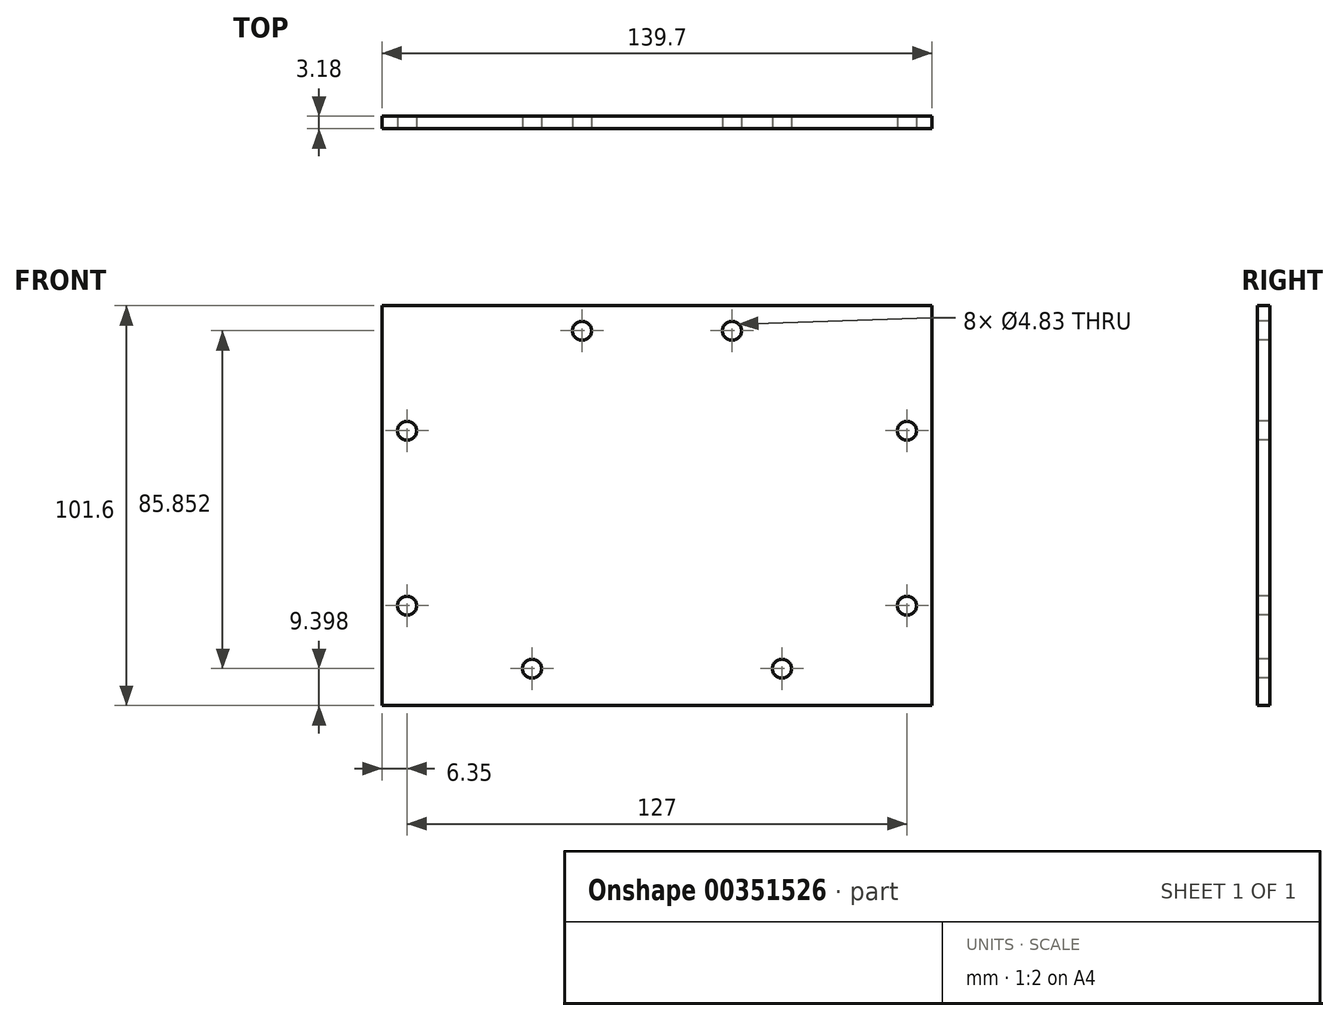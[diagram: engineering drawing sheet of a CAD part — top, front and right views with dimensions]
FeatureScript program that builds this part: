
annotation { "Feature Type Name" : "Feature", "Feature Type Description" : "" }
export const myFeature = defineFeature(function(context is Context, id is Id, definition is map)
    precondition{}
    {
        {
            var Q0;
            Q0=qCreatedBy(makeId("Front.planeOp"),FACE);
            var sketch = newSketch(context, id + "F0", { "sketchPlane" : qUnion([Q0])});
            skLineSegment(sketch, "E0.bottom", {"start": v(69.85, 50.8) * mm, "end": v(-69.85, 50.8) * mm});
            skLineSegment(sketch, "E0.top", {"start": v(69.85, -50.8) * mm, "end": v(-69.85, -50.8) * mm});
            skLineSegment(sketch, "E0.left", {"start": v(69.85, 50.8) * mm, "end": v(69.85, -50.8) * mm});
            skLineSegment(sketch, "E0.right", {"start": v(-69.85, 50.8) * mm, "end": v(-69.85, -50.8) * mm});
            skPoint(sketch, "E0.middle", {"position": v(0, 0) * mm});
            skSolve(sketch);
        }
        {
            var Q0;
            Q0 = qSketchRegion(id + "F0", true);
            extrude(context, id + "F1", {"entities" : qUnion([Q0]), "depth" : 3.17 * mm, "symmetric" : true});
        }
        {
            var Q0;
            Q0=makeQuery(id+"F1.opExtrude","CAP_FACE",FACE,{"disambiguationData":[OSD([sQuery(id+"F0.wireOp",EDGE,"E0.bottom"),sQuery(id+"F0.wireOp",EDGE,"E0.top"),sQuery(id+"F0.wireOp",EDGE,"E0.left"),sQuery(id+"F0.wireOp",EDGE,"E0.right")])],"isStart":false});
            var sketch = newSketch(context, id + "F2", { "sketchPlane" : qUnion([Q0])});
            skCircle(sketch, "E1", {"center": v(-19.05, 44.45) * mm, "radius": 2.41 * mm});
            skCircle(sketch, "E2", {"center": v(19.05, 44.45) * mm, "radius": 2.41 * mm});
            skSolve(sketch);
        }
        {
            var Q0;
            Q0 = qSketchRegion(id + "F2", true);
            var Q1;
            Q1=makeQuery(id+"F1.opExtrude","CAP_FACE",FACE,{"disambiguationData":[OSD([sQuery(id+"F0.wireOp",EDGE,"E0.bottom"),sQuery(id+"F0.wireOp",EDGE,"E0.top"),sQuery(id+"F0.wireOp",EDGE,"E0.left"),sQuery(id+"F0.wireOp",EDGE,"E0.right")])],"isStart":true});
            extrude(context, id + "F3", {"entities" : qUnion([Q0]), "operationType" : NewBodyOperationType.REMOVE, "endBound" : BoundingType.UP_TO_SURFACE, "oppositeDirection" : true, "endBoundEntityFace" : qUnion([Q1]), "depth" : 25.4 * mm});
        }
        {
            var Q0;
            Q0=makeQuery(id+"F1.opExtrude","CAP_FACE",FACE,{"disambiguationData":[OSD([sQuery(id+"F0.wireOp",EDGE,"E0.bottom"),sQuery(id+"F0.wireOp",EDGE,"E0.top"),sQuery(id+"F0.wireOp",EDGE,"E0.left"),sQuery(id+"F0.wireOp",EDGE,"E0.right")])],"isStart":false});
            var sketch = newSketch(context, id + "F4", { "sketchPlane" : qUnion([Q0])});
            skCircle(sketch, "E3", {"center": v(-31.75, -41.4) * mm, "radius": 2.41 * mm});
            skCircle(sketch, "E4", {"center": v(31.75, -41.4) * mm, "radius": 2.41 * mm});
            skSolve(sketch);
        }
        {
            var Q0;
            Q0 = qSketchRegion(id + "F4", true);
            var Q1;
            Q1=makeQuery(id+"F1.opExtrude","CAP_FACE",FACE,{"disambiguationData":[OSD([sQuery(id+"F0.wireOp",EDGE,"E0.bottom"),sQuery(id+"F0.wireOp",EDGE,"E0.top"),sQuery(id+"F0.wireOp",EDGE,"E0.left"),sQuery(id+"F0.wireOp",EDGE,"E0.right")])],"isStart":true});
            extrude(context, id + "F5", {"entities" : qUnion([Q0]), "operationType" : NewBodyOperationType.REMOVE, "endBound" : BoundingType.UP_TO_SURFACE, "oppositeDirection" : true, "endBoundEntityFace" : qUnion([Q1]), "depth" : 25.4 * mm});
        }
        {
            var Q0;
            Q0=makeQuery(id+"F1.opExtrude","CAP_FACE",FACE,{"disambiguationData":[OSD([sQuery(id+"F0.wireOp",EDGE,"E0.bottom"),sQuery(id+"F0.wireOp",EDGE,"E0.top"),sQuery(id+"F0.wireOp",EDGE,"E0.left"),sQuery(id+"F0.wireOp",EDGE,"E0.right")])],"isStart":false});
            var sketch = newSketch(context, id + "F6", { "sketchPlane" : qUnion([Q0])});
            skCircle(sketch, "E5", {"center": v(-63.5, -25.4) * mm, "radius": 2.41 * mm});
            skCircle(sketch, "E6", {"center": v(-63.5, 19.05) * mm, "radius": 2.41 * mm});
            skCircle(sketch, "E7", {"center": v(63.5, 19.05) * mm, "radius": 2.41 * mm});
            skCircle(sketch, "E8", {"center": v(63.5, -25.4) * mm, "radius": 2.41 * mm});
            skSolve(sketch);
        }
        {
            var Q0;
            Q0 = qSketchRegion(id + "F6", true);
            var Q1;
            Q1=makeQuery(id+"F1.opExtrude","CAP_FACE",FACE,{"disambiguationData":[OSD([sQuery(id+"F0.wireOp",EDGE,"E0.bottom"),sQuery(id+"F0.wireOp",EDGE,"E0.top"),sQuery(id+"F0.wireOp",EDGE,"E0.left"),sQuery(id+"F0.wireOp",EDGE,"E0.right")])],"isStart":true});
            extrude(context, id + "F7", {"entities" : qUnion([Q0]), "operationType" : NewBodyOperationType.REMOVE, "endBound" : BoundingType.UP_TO_SURFACE, "oppositeDirection" : true, "endBoundEntityFace" : qUnion([Q1]), "depth" : 25.4 * mm});
        }
    });
